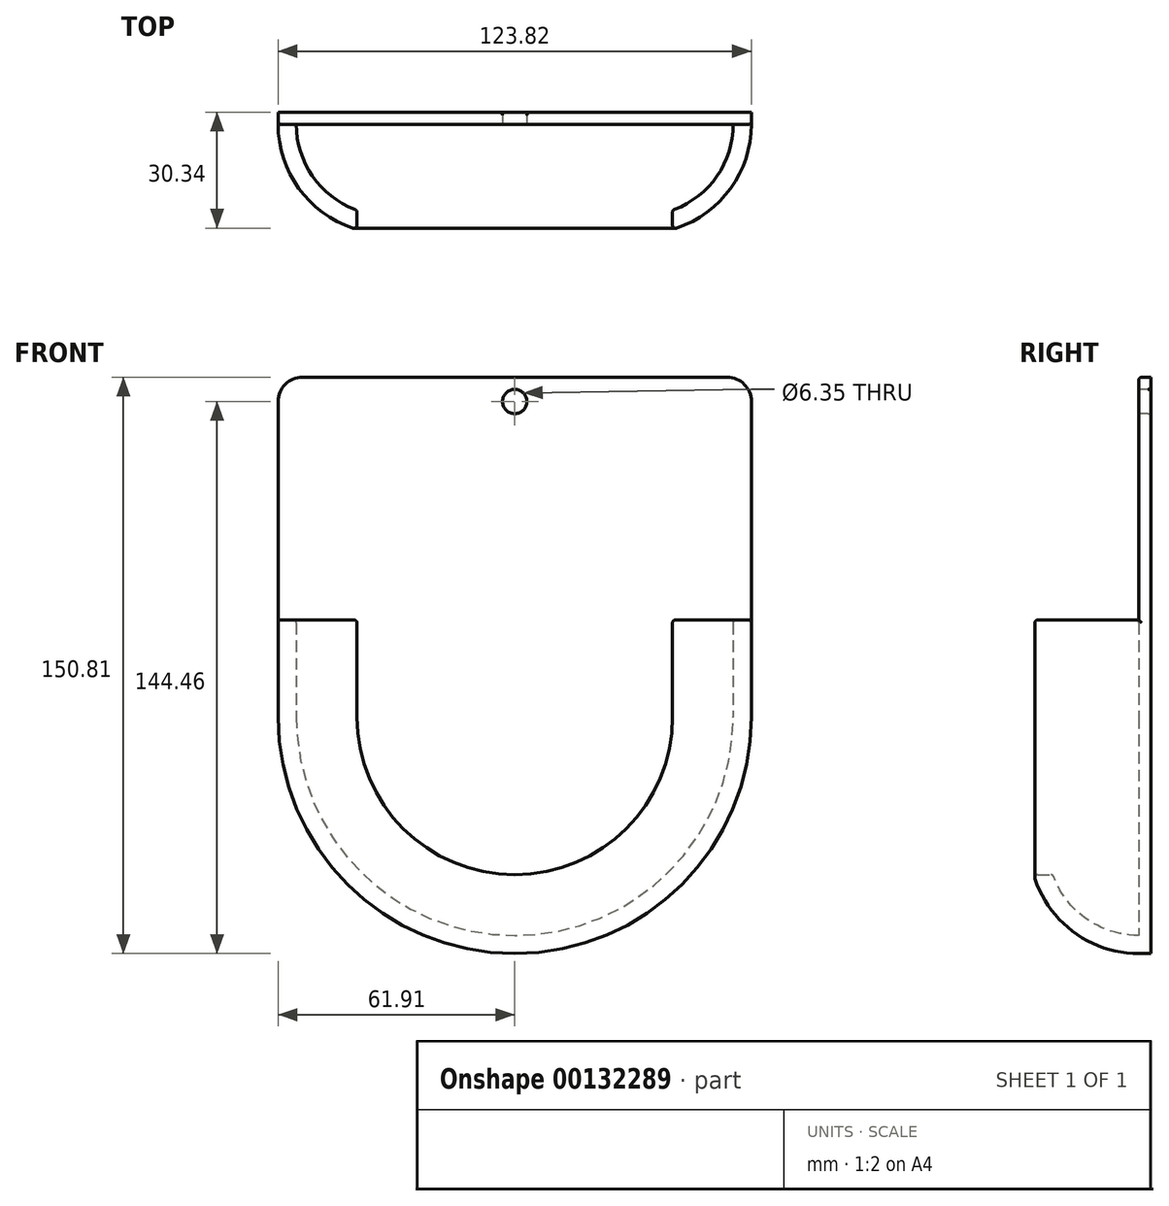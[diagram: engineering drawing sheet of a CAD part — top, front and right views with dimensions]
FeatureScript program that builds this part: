
annotation { "Feature Type Name" : "Feature", "Feature Type Description" : "" }
export const myFeature = defineFeature(function(context is Context, id is Id, definition is map)
    precondition{}
    {
        {
            var Q0;
            Q0=qCreatedBy(makeId("Front.planeOp"),FACE);
            var sketch = newSketch(context, id + "F0", { "sketchPlane" : qUnion([Q0])});
            skCircle(sketch, "E0", {"center": v(0, 0) * mm, "radius": 61.91 * mm});
            skLineSegment(sketch, "E1.bottom", {"start": v(-61.91, 0) * mm, "end": v(61.91, 0) * mm});
            skLineSegment(sketch, "E1.top", {"start": v(-61.91, 88.9) * mm, "end": v(61.91, 88.9) * mm});
            skLineSegment(sketch, "E1.left", {"start": v(-61.91, 0) * mm, "end": v(-61.91, 88.9) * mm});
            skLineSegment(sketch, "E1.right", {"start": v(61.91, 0) * mm, "end": v(61.91, 88.9) * mm});
            skSolve(sketch);
        }
        {
            var Q0;
            {var subQ0=sQuery(id+"F0.wireOp",EDGE,"E1.bottom");Q0=makeQuery(id+"F0.imprint","IMPRINT",FACE,{"disambiguationData":[TD([[makeQuery(id+"F0.imprint","IMPRINT",EDGE,{"derivedFrom":subQ0}),-1.0]])]});}
            var Q1;
            Q1=makeQuery(id+"F0.imprint","IMPRINT",FACE,{"disambiguationData":[TD([[makeQuery(id+"F0.imprint","IMPRINT",EDGE,{"derivedFrom":sQuery(id+"F0.wireOp",EDGE,"E1.top")}),-1.0]])]});
            var Q2;
            {var subQ0=sQuery(id+"F0.wireOp",EDGE,"E1.bottom");Q2=makeQuery(id+"F0.imprint","IMPRINT",FACE,{"disambiguationData":[TD([[makeQuery(id+"F0.imprint","IMPRINT",EDGE,{"derivedFrom":subQ0}),1.0]])]});}
            extrude(context, id + "F1", {"entities" : qUnion([Q0, Q1, Q2]), "depth" : 3.17 * mm});
        }
        {
            var Q0;
            Q0=qCreatedBy(makeId("Top.planeOp"),FACE);
            var sketch = newSketch(context, id + "F2", { "sketchPlane" : qUnion([Q0])});
            skArc(sketch, "E2", {"start": v(-61.91, -3.18) * mm, "mid": v(-56.18, -20.35) * mm, "end": v(-41.28, -30.63) * mm});
            skArc(sketch, "E3", {"start": v(-57.15, -3.17) * mm, "mid": v(-52.78, -16.92) * mm, "end": v(-41.28, -25.63) * mm});
            skLineSegment(sketch, "E4", {"start": v(-61.91, -3.18) * mm, "end": v(-57.15, -3.17) * mm});
            skLineSegment(sketch, "E5", {"start": v(-41.28, -30.63) * mm, "end": v(-41.28, -25.63) * mm});
            skSolve(sketch);
        }
        {
            var Q0;
            Q0=qSketchRegion(id+"F2",true);
            var Q1;
            Q1=makeQuery(id+"F1.opExtrude","SWEPT_FACE",FACE,{"disambiguationData":[OSD([sQuery(id+"F0.wireOp",EDGE,"E0")])]});
            revolve(context, id + "F3", {"operationType" : NewBodyOperationType.ADD, "entities" : qUnion([Q0]), "axis" : qUnion([Q1]), "revolveType" : RevolveType.ONE_DIRECTION, "oppositeDirection" : true, "angle" : 180 * degree});
        }
        {
            var Q0;
            Q0=makeQuery(id+"F3.opRevolve","CAP_FACE",FACE,{"disambiguationData":[OSD([sQuery(id+"F2.wireOp",EDGE,"E2"),sQuery(id+"F2.wireOp",EDGE,"E3"),sQuery(id+"F2.wireOp",EDGE,"E4"),sQuery(id+"F2.wireOp",EDGE,"5gcFSOU7-eLQE-9mHl-yvXb-bSVD1MqFUzp8.bottom"),sQuery(id+"F2.wireOp",EDGE,"5gcFSOU7-eLQE-9mHl-yvXb-bSVD1MqFUzp8.top"),sQuery(id+"F2.wireOp",EDGE,"5gcFSOU7-eLQE-9mHl-yvXb-bSVD1MqFUzp8.right")])],"isStart":true});
            var Q1;
            Q1=makeQuery(id+"F3.opRevolve","CAP_FACE",FACE,{"disambiguationData":[OSD([sQuery(id+"F2.wireOp",EDGE,"E2"),sQuery(id+"F2.wireOp",EDGE,"E3"),sQuery(id+"F2.wireOp",EDGE,"E4"),sQuery(id+"F2.wireOp",EDGE,"5gcFSOU7-eLQE-9mHl-yvXb-bSVD1MqFUzp8.bottom"),sQuery(id+"F2.wireOp",EDGE,"5gcFSOU7-eLQE-9mHl-yvXb-bSVD1MqFUzp8.top"),sQuery(id+"F2.wireOp",EDGE,"5gcFSOU7-eLQE-9mHl-yvXb-bSVD1MqFUzp8.right")])],"isStart":false});
            extrude(context, id + "F4", {"entities" : qUnion([Q0, Q1]), "operationType" : NewBodyOperationType.ADD, "depth" : 25.4 * mm});
        }
        {
            var Q0;
            Q0=makeQuery(id+"F3.opRevolve","SWEPT_EDGE",EDGE,{"disambiguationData":[OSD([sQuery(id+"F2.wireOp",EDGE,"5gcFSOU7-eLQE-9mHl-yvXb-bSVD1MqFUzp8.bottom"),sQuery(id+"F2.wireOp",EDGE,"5gcFSOU7-eLQE-9mHl-yvXb-bSVD1MqFUzp8.right")])]});
            var Q1;
            Q1=makeQuery(id+"F3.opRevolve","SWEPT_EDGE",EDGE,{"disambiguationData":[OSD([sQuery(id+"F2.wireOp",EDGE,"E3"),sQuery(id+"F2.wireOp",EDGE,"E4")])]});
            var Q2;
            Q2=makeQuery(id+"F3.opRevolve","SWEPT_EDGE",EDGE,{"disambiguationData":[OSD([sQuery(id+"F2.wireOp",EDGE,"5gcFSOU7-eLQE-9mHl-yvXb-bSVD1MqFUzp8.top"),sQuery(id+"F2.wireOp",EDGE,"5gcFSOU7-eLQE-9mHl-yvXb-bSVD1MqFUzp8.right")])]});
            var Q3;
            Q3=makeQuery(id+"F3.opRevolve","SWEPT_EDGE",EDGE,{"disambiguationData":[OSD([sQuery(id+"F2.wireOp",EDGE,"E2"),sQuery(id+"F2.wireOp",EDGE,"5gcFSOU7-eLQE-9mHl-yvXb-bSVD1MqFUzp8.bottom"),sQuery(id+"F2.wireOp",EDGE,"5gcFSOU7-eLQE-9mHl-yvXb-bSVD1MqFUzp8.left")])]});
            var Q4;
            {var subQ0=sQuery(id+"F2.wireOp",EDGE,"E3");Q4=makeQuery(id+"F4.opExtrude","CAP_EDGE",EDGE,{"disambiguationData":[OSD([subQ0]),TDD([makeQuery(id+"F3.opRevolve","CAP_EDGE",EDGE,{"disambiguationData":[OSD([subQ0])],"isStart":true})])],"isStart":false});}
            var Q5;
            {var subQ0=sQuery(id+"F2.wireOp",EDGE,"E3");Q5=makeQuery(id+"F4.opExtrude","CAP_EDGE",EDGE,{"disambiguationData":[OSD([subQ0]),TDD([makeQuery(id+"F3.opRevolve","CAP_EDGE",EDGE,{"disambiguationData":[OSD([subQ0])],"isStart":false})])],"isStart":false});}
            var Q6;
            {var subQ0=sQuery(id+"F2.wireOp",EDGE,"E5");Q6=makeQuery(id+"F4.opExtrude","CAP_EDGE",EDGE,{"disambiguationData":[OSD([subQ0]),TDD([makeQuery(id+"F3.opRevolve","CAP_EDGE",EDGE,{"disambiguationData":[OSD([subQ0])],"isStart":true})])],"isStart":false});}
            var Q7;
            {var subQ0=sQuery(id+"F2.wireOp",EDGE,"E5");Q7=makeQuery(id+"F4.opExtrude","CAP_EDGE",EDGE,{"disambiguationData":[OSD([subQ0]),TDD([makeQuery(id+"F3.opRevolve","CAP_EDGE",EDGE,{"disambiguationData":[OSD([subQ0])],"isStart":false})])],"isStart":false});}
            fillet(context, id + "F5", {"entities" : qUnion([Q0, Q1, Q2, Q3, Q4, Q5, Q6, Q7]), "radius" : 0.8 * mm, "tangentPropagation" : true, "allowEdgeOverflow" : false});
        }
        {
            var Q0;
            {var subQ0=sQuery(id+"F2.wireOp",EDGE,"E2");Q0=makeQuery(id+"F4.opExtrude","CAP_EDGE",EDGE,{"disambiguationData":[OSD([subQ0]),TDD([makeQuery(id+"F3.opRevolve","CAP_EDGE",EDGE,{"disambiguationData":[OSD([subQ0])],"isStart":true})])],"isStart":false});}
            var Q1;
            {var subQ0=sQuery(id+"F2.wireOp",EDGE,"E2");Q1=makeQuery(id+"F4.opExtrude","CAP_EDGE",EDGE,{"disambiguationData":[OSD([subQ0]),TDD([makeQuery(id+"F3.opRevolve","CAP_EDGE",EDGE,{"disambiguationData":[OSD([subQ0])],"isStart":false})])],"isStart":false});}
            var Q2;
            {var subQ0=sQuery(id+"F2.wireOp",EDGE,"E5");var subQ1=sQuery(id+"F2.wireOp",EDGE,"E3");Q2=makeQuery(id+"F4.opExtrude","SWEPT_EDGE",EDGE,{"disambiguationData":[OSD([subQ1,subQ0]),TDD([makeQuery(id+"F3.opRevolve","CAP_VERTEX",VERTEX,{"disambiguationData":[OSD([subQ1,subQ0])],"isStart":true})])]});}
            fillet(context, id + "F6", {"entities" : qUnion([Q0, Q1, Q2]), "radius" : 0.8 * mm, "tangentPropagation" : true, "allowEdgeOverflow" : false});
        }
        {
            var Q0;
            Q0=makeQuery(id+"F1.opExtrude","SWEPT_EDGE",EDGE,{"disambiguationData":[OSD([sQuery(id+"F0.wireOp",EDGE,"E1.top"),sQuery(id+"F0.wireOp",EDGE,"E1.right")])]});
            var Q1;
            Q1=makeQuery(id+"F1.opExtrude","SWEPT_EDGE",EDGE,{"disambiguationData":[OSD([sQuery(id+"F0.wireOp",EDGE,"E1.top"),sQuery(id+"F0.wireOp",EDGE,"E1.left")])]});
            fillet(context, id + "F7", {"entities" : qUnion([Q0, Q1]), "radius" : 6.35 * mm, "allowEdgeOverflow" : false});
        }
        {
            var Q0;
            Q0=makeQuery(id+"F1.opExtrude","CAP_EDGE",EDGE,{"disambiguationData":[OSD([sQuery(id+"F0.wireOp",EDGE,"E1.top")])],"isStart":false});
            var Q1;
            {var subQ0=sQuery(id+"F0.wireOp",EDGE,"E1.left");var subQ1=sQuery(id+"F0.wireOp",EDGE,"E1.top");Q1=makeQuery(id+"F7.opFillet","BLEND_EDGE",EDGE,{"blendedFrom":[makeQuery(id+"F1.opExtrude","SWEPT_EDGE",EDGE,{"disambiguationData":[OSD([subQ1,subQ0])]}),makeQuery(id+"F1.opExtrude","CAP_FACE",FACE,{"disambiguationData":[OSD([sQuery(id+"F0.wireOp",EDGE,"E0"),subQ1,subQ0,sQuery(id+"F0.wireOp",EDGE,"E1.right")])],"isStart":false})],"blendedInto":[makeQuery(id+"F1.opExtrude","CAP_FACE",FACE,{"disambiguationData":[OSD([sQuery(id+"F0.wireOp",EDGE,"E0"),subQ1,subQ0,sQuery(id+"F0.wireOp",EDGE,"E1.right")])],"isStart":false})]});}
            var Q2;
            {var subQ0=sQuery(id+"F0.wireOp",EDGE,"E1.right");var subQ1=sQuery(id+"F0.wireOp",EDGE,"E1.top");Q2=makeQuery(id+"F7.opFillet","BLEND_EDGE",EDGE,{"blendedFrom":[makeQuery(id+"F1.opExtrude","SWEPT_EDGE",EDGE,{"disambiguationData":[OSD([subQ1,subQ0])]}),makeQuery(id+"F1.opExtrude","CAP_FACE",FACE,{"disambiguationData":[OSD([sQuery(id+"F0.wireOp",EDGE,"E0"),subQ1,sQuery(id+"F0.wireOp",EDGE,"E1.left"),subQ0])],"isStart":false})],"blendedInto":[makeQuery(id+"F1.opExtrude","CAP_FACE",FACE,{"disambiguationData":[OSD([sQuery(id+"F0.wireOp",EDGE,"E0"),subQ1,sQuery(id+"F0.wireOp",EDGE,"E1.left"),subQ0])],"isStart":false})]});}
            fillet(context, id + "F8", {"entities" : qUnion([Q0, Q1, Q2]), "radius" : 0.8 * mm, "tangentPropagation" : true, "allowEdgeOverflow" : false});
        }
        {
            var Q0;
            Q0=makeQuery(id+"F1.opExtrude","CAP_FACE",FACE,{"disambiguationData":[OSD([sQuery(id+"F0.wireOp",EDGE,"E0"),sQuery(id+"F0.wireOp",EDGE,"E1.top"),sQuery(id+"F0.wireOp",EDGE,"E1.left"),sQuery(id+"F0.wireOp",EDGE,"E1.right")])],"isStart":false});
            var sketch = newSketch(context, id + "F9", { "sketchPlane" : qUnion([Q0])});
            skCircle(sketch, "E6", {"center": v(0, 82.55) * mm, "radius": 3.18 * mm});
            skSolve(sketch);
        }
        {
            var Q0;
            Q0=qSketchRegion(id+"F9",true);
            extrude(context, id + "F10", {"entities" : qUnion([Q0]), "operationType" : NewBodyOperationType.REMOVE, "endBound" : BoundingType.THROUGH_ALL, "oppositeDirection" : true, "depth" : 25.4 * mm});
        }
        {
            var Q0;
            Q0=makeQuery(id+"F10.boolean.opBoolean","COPY",EDGE,{"derivedFrom":makeQuery(id+"F10.opExtrude","CAP_EDGE",EDGE,{"disambiguationData":[OSD([sQuery(id+"F9.wireOp",EDGE,"E6")])],"isStart":true})});
            var Q1;
            Q1=makeQuery(id+"F10.boolean.opBoolean","INTERSECT",EDGE,{"derivedFrom":[makeQuery(id+"F1.opExtrude","CAP_FACE",FACE,{"disambiguationData":[OSD([sQuery(id+"F0.wireOp",EDGE,"E0"),sQuery(id+"F0.wireOp",EDGE,"E1.top"),sQuery(id+"F0.wireOp",EDGE,"E1.left"),sQuery(id+"F0.wireOp",EDGE,"E1.right")])],"isStart":true}),makeQuery(id+"F10.opExtrude","SWEPT_FACE",FACE,{"disambiguationData":[OSD([sQuery(id+"F9.wireOp",EDGE,"E6")])]})]});
            fillet(context, id + "F11", {"entities" : qUnion([Q0, Q1]), "radius" : 0.8 * mm, "tangentPropagation" : true, "allowEdgeOverflow" : false});
        }
    });
